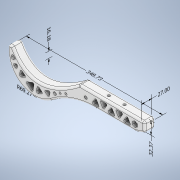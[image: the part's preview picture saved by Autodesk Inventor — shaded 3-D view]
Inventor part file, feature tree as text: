
AUTODESK INVENTOR PART (.ipt)
format: ipt  version: 2020 (Build 240168000, 168)  size: 437,248 bytes
history: native  units: in
note: dims shown in document units (in); Inventor stores cm internally (conversion verified against a paired STEP export)
features: other x6, hole x2, sketch x1
ambient origin geometry x8: Origin, YZ Plane, XZ Plane, XY Plane, X Axis, Y Axis, Z Axis, Center Point
bodies: Solid2 (feature_tree), Solid1 (feature_tree)
feature tree (9):
  other  "Annotations"
  hole  "Hole2"  [1 undecoded]
  sketch  "Sketch1"  dims[d3=0.2598in d4=0.2362in d5=0.1575in d6=0.0787in d7=90.0deg d8=0.315in d9=0.0in d10=0.3902in d11=0.3656in d12=1.063in d13=0.2234in d14=0.1899in d15=1.2744in d18=0.2257in d19=13.7294in d20=0.3753in d21=0.6372in d22=0.1553in d23=0.1591in d24=0.2657in d25=2.7271in]
  hole  "Hole1"  [1 undecoded]
  other  "Linear Dimension 3"
  other  "Linear Dimension 4"
  other  "Linear Dimension 5"
  other  "Linear Dimension 6"
  other  "Radial Dimension 1"
note: 2 required parameter values undecoded (feature->parameter linkage not recoverable at this tier; creation-order binding heuristic only, values carry confidence <= 0.55)
